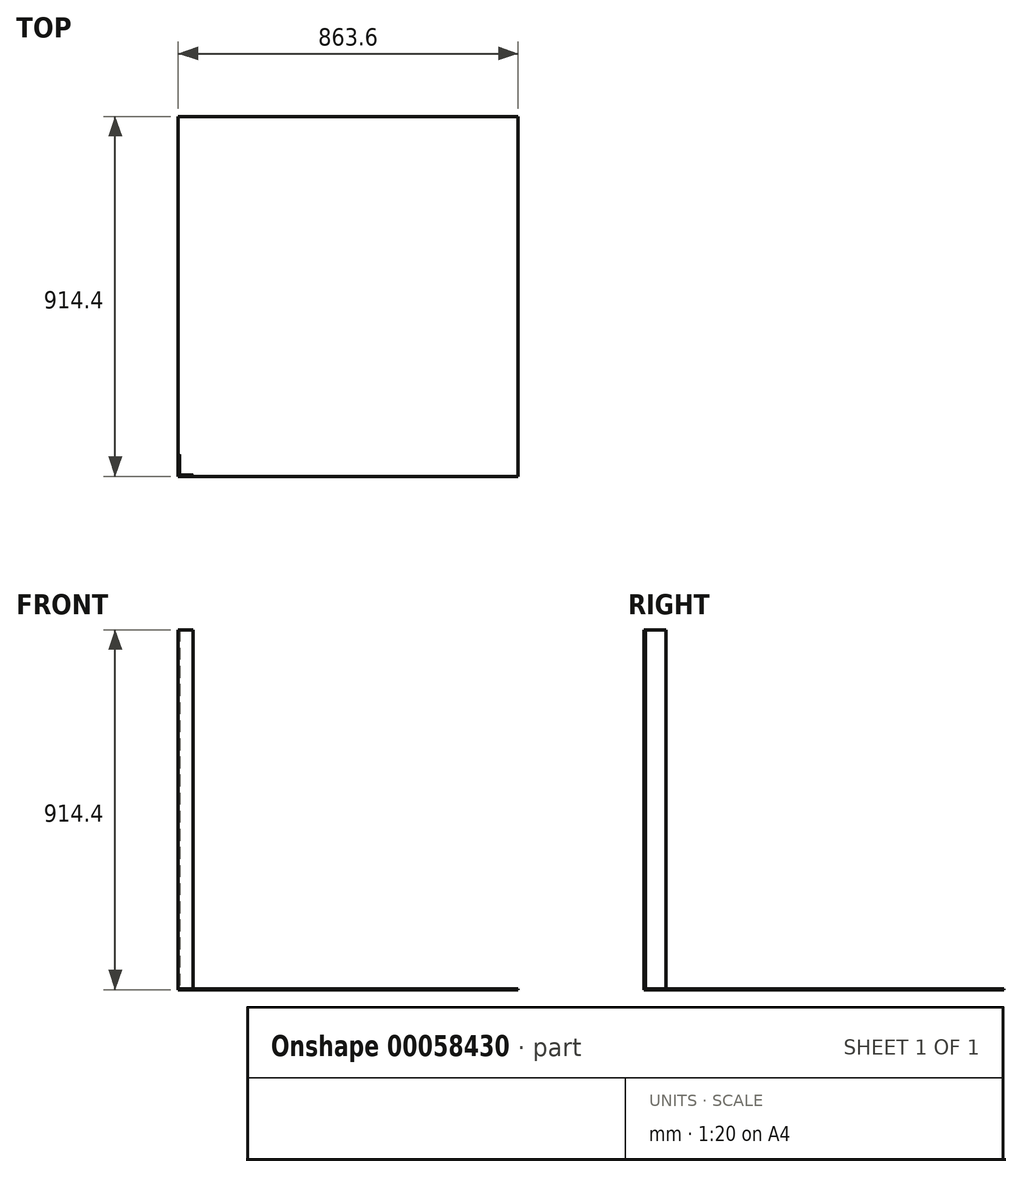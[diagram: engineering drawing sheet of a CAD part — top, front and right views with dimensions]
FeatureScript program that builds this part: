
annotation { "Feature Type Name" : "Feature", "Feature Type Description" : "" }
export const myFeature = defineFeature(function(context is Context, id is Id, definition is map)
    precondition{}
    {
        {
            var Q0;
            Q0=qCreatedBy(makeId("Top.planeOp"),FACE);
            var sketch = newSketch(context, id + "F0", { "sketchPlane" : qUnion([Q0])});
            skLineSegment(sketch, "E0", {"start": v(0, 0) * mm, "end": v(38.1, 0) * mm});
            skLineSegment(sketch, "E1", {"start": v(38.1, 0) * mm, "end": v(38.1, 1.59) * mm});
            skLineSegment(sketch, "E2", {"start": v(36.51, 3.18) * mm, "end": v(3.18, 3.17) * mm});
            skLineSegment(sketch, "E3", {"start": v(3.18, 3.17) * mm, "end": v(3.18, 53.92) * mm});
            skLineSegment(sketch, "E4", {"start": v(1.59, 55.5) * mm, "end": v(0, 55.5) * mm});
            skLineSegment(sketch, "E5", {"start": v(0, 55.5) * mm, "end": v(0, 0) * mm});
            skPoint(sketch, "E6.visualSharp", {"position": v(38.1, 3.18) * mm});
            skArc(sketch, "E6.filletArc", {"start": v(38.1, 1.59) * mm, "mid": v(37.64, 2.71) * mm, "end": v(36.51, 3.17) * mm});
            skPoint(sketch, "E7.visualSharp", {"position": v(3.18, 55.5) * mm});
            skArc(sketch, "E7.filletArc", {"start": v(3.18, 53.92) * mm, "mid": v(2.71, 55.04) * mm, "end": v(1.59, 55.5) * mm});
            skSolve(sketch);
        }
        {
            var Q0;
            Q0 = qSketchRegion(id + "F0", true);
            extrude(context, id + "F1", {"entities" : qUnion([Q0]), "depth" : 914.4 * mm});
        }
        {
            var Q0;
            Q0=qCreatedBy(makeId("Top.planeOp"),FACE);
            var sketch = newSketch(context, id + "F2", { "sketchPlane" : qUnion([Q0])});
            skLineSegment(sketch, "E8.bottom", {"start": v(0, 0) * mm, "end": v(863.6, 0) * mm});
            skLineSegment(sketch, "E8.top", {"start": v(0, 914.4) * mm, "end": v(863.6, 914.4) * mm});
            skLineSegment(sketch, "E8.left", {"start": v(0, 0) * mm, "end": v(0, 914.4) * mm});
            skLineSegment(sketch, "E8.right", {"start": v(863.6, 0) * mm, "end": v(863.6, 914.4) * mm});
            skSolve(sketch);
        }
        {
            var Q0;
            Q0 = qSketchRegion(id + "F2", true);
            extrude(context, id + "F3", {"entities" : qUnion([Q0]), "depth" : 1.59 * mm});
        }
    });
